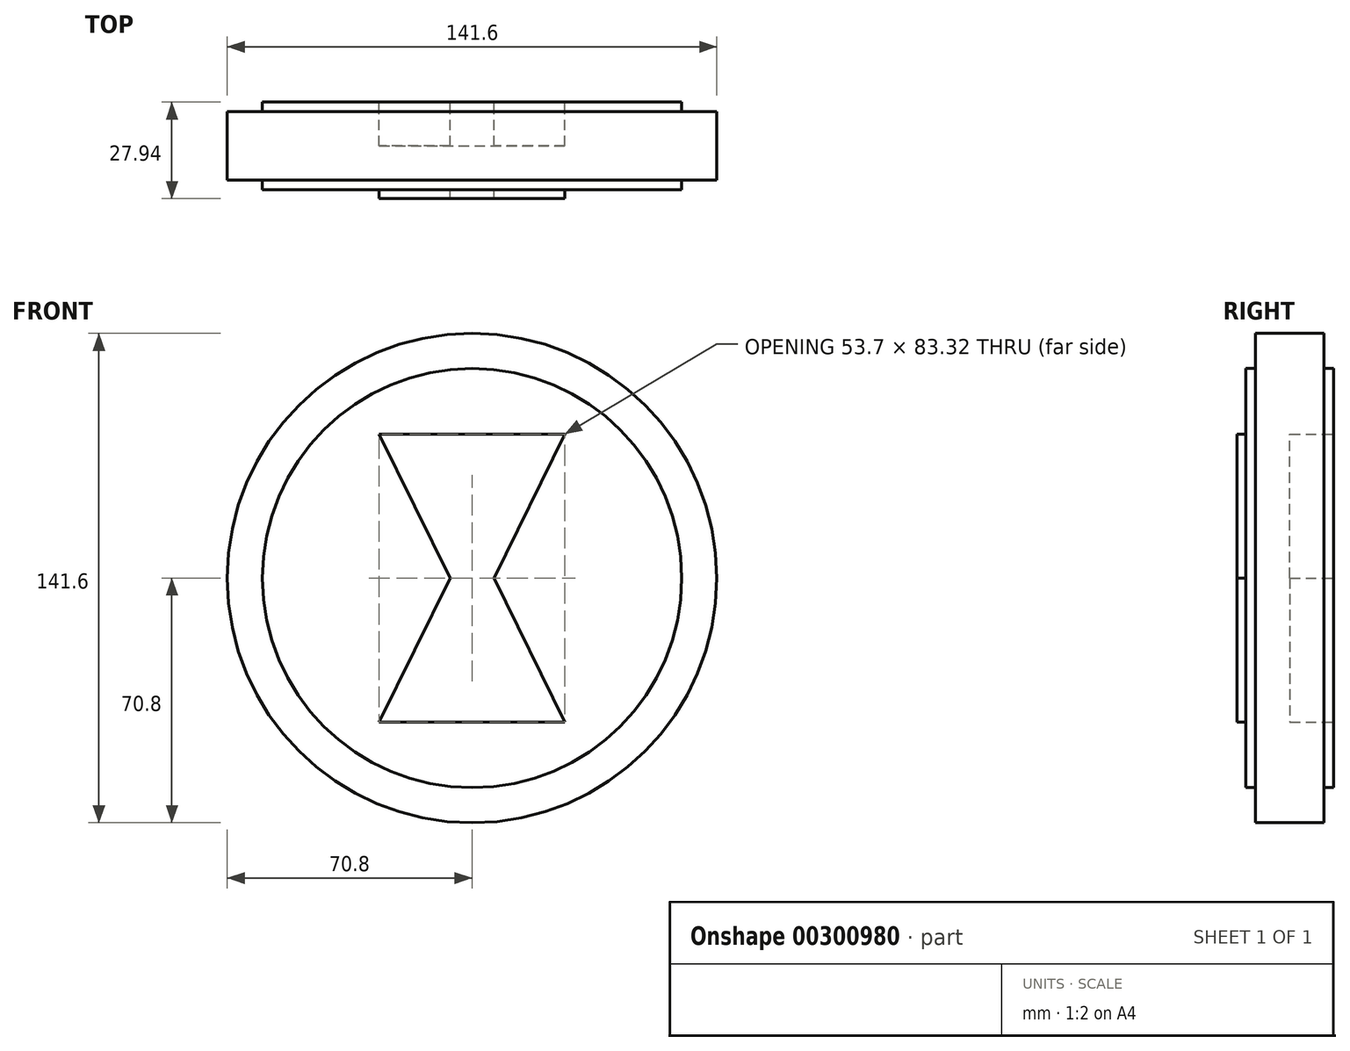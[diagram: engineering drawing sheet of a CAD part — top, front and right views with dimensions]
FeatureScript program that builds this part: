
annotation { "Feature Type Name" : "Feature", "Feature Type Description" : "" }
export const myFeature = defineFeature(function(context is Context, id is Id, definition is map)
    precondition{}
    {
        {
            var Q0;
            Q0=qCreatedBy(makeId("Front.planeOp"),FACE);
            var sketch = newSketch(context, id + "F0", { "sketchPlane" : qUnion([Q0])});
            skCircle(sketch, "E0", {"center": v(0, 0) * mm, "radius": 70.8 * mm});
            skCircle(sketch, "E1", {"center": v(0, 0) * mm, "radius": 60.64 * mm});
            skLineSegment(sketch, "E2", {"start": v(-26.85, 41.66) * mm, "end": v(26.85, 41.66) * mm});
            skLineSegment(sketch, "E3", {"start": v(26.85, 41.66) * mm, "end": v(6.35, 0) * mm});
            skLineSegment(sketch, "E4", {"start": v(6.35, 0) * mm, "end": v(26.85, -41.66) * mm});
            skLineSegment(sketch, "E5", {"start": v(26.85, -41.66) * mm, "end": v(-26.85, -41.66) * mm});
            skLineSegment(sketch, "E6", {"start": v(-26.85, -41.66) * mm, "end": v(-6.35, 0) * mm});
            skLineSegment(sketch, "E7", {"start": v(-6.35, 0) * mm, "end": v(-26.85, 41.66) * mm});
            skSolve(sketch);
        }
        {
            var Q0;
            Q0=makeQuery(id+"F0.imprint","IMPRINT",FACE,{"disambiguationData":[TD([[makeQuery(id+"F0.imprint","IMPRINT",EDGE,{"derivedFrom":sQuery(id+"F0.wireOp",EDGE,"E0")}),1.0]])]});
            extrude(context, id + "F1", {"entities" : qUnion([Q0]), "endBound" : BoundingType.SYMMETRIC, "depth" : 19.8 * mm});
        }
        {
            var Q0;
            Q0=makeQuery(id+"F0.imprint","IMPRINT",FACE,{"disambiguationData":[TD([[makeQuery(id+"F0.imprint","IMPRINT",EDGE,{"derivedFrom":sQuery(id+"F0.wireOp",EDGE,"E1")}),1.0]])]});
            extrude(context, id + "F2", {"entities" : qUnion([Q0]), "operationType" : NewBodyOperationType.ADD, "endBound" : BoundingType.SYMMETRIC, "depth" : 25.4 * mm});
        }
        {
            var Q0;
            Q0=makeQuery(id+"F0.imprint","IMPRINT",FACE,{"disambiguationData":[TD([[makeQuery(id+"F0.imprint","IMPRINT",EDGE,{"derivedFrom":sQuery(id+"F0.wireOp",EDGE,"E2")}),-1.0]])]});
            extrude(context, id + "F3", {"entities" : qUnion([Q0]), "operationType" : NewBodyOperationType.ADD, "depth" : 15.24 * mm});
        }
    });
